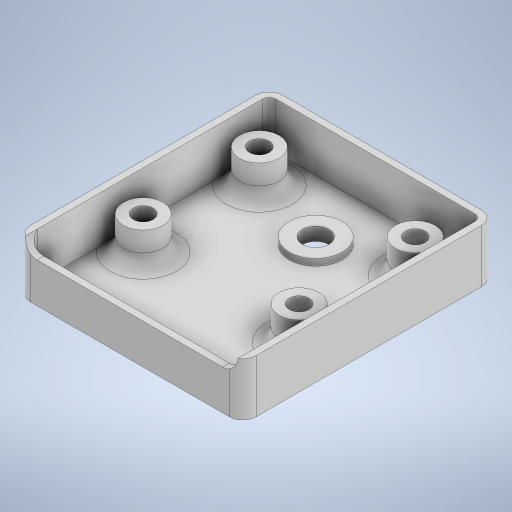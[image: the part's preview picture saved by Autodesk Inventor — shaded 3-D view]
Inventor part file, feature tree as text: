
AUTODESK INVENTOR PART (.ipt)
format: ipt  version: 2024.2 (Build 282272000, 272)  size: 377,344 bytes
history: native  units: mm
features: extrude x5, sketch x5, fillet x4, shell x1
ambient origin geometry x8: Origin, YZ Plane, XZ Plane, XY Plane, X Axis, Y Axis, Z Axis, Center Point
bodies: Solid1 (feature_tree)
feature tree (15):
  extrude  "Extrusion1"  Depth=34.0mm
  shell  "Shell1"  Thickness=8.0mm
  extrude  "Extrusion2"  Depth=1.0mm
  fillet  "Fillet1"  Radius=6.0mm
  extrude  "Extrusion3"  Depth=6.0mm
  extrude  "Extrusion4"  Depth=17.5mm
  extrude  "Extrusion5"  Depth=1.0mm
  fillet  "Fillet2"  Radius=5.0mm
  fillet  "Fillet3"  Radius=3.0mm
  fillet  "Fillet4"  Radius=3.0mm
  sketch  "Sketch1"  dims[d0=38.0mm d1=34.0mm d4=8.0mm d5=0.0mm]
  sketch  "Sketch2"  dims[d6=1.0mm d7=6.0mm d8=6.0mm]
  sketch  "Sketch3"  dims[d9=6.0mm d10=6.0mm]
  sketch  "Sketch4"  dims[d11=13.0mm d12=17.5mm]
  sketch  "Sketch5"  dims[d13=4.0mm d14=23.5mm d15=5.0mm d16=0.0mm d17=3.0mm d18=3.0mm d19=3.0mm d20=3.0mm d21=2.0mm d22=10.0mm d23=4.0mm d24=4.0mm d25=0.0mm d26=8.0mm d27=1.0mm d28=0.0mm d30=1.0mm d31=1.0mm d32=2.0mm d33=1.0mm d34=0.0mm d35=2.0mm d36=2.0mm d37=1.0mm]
